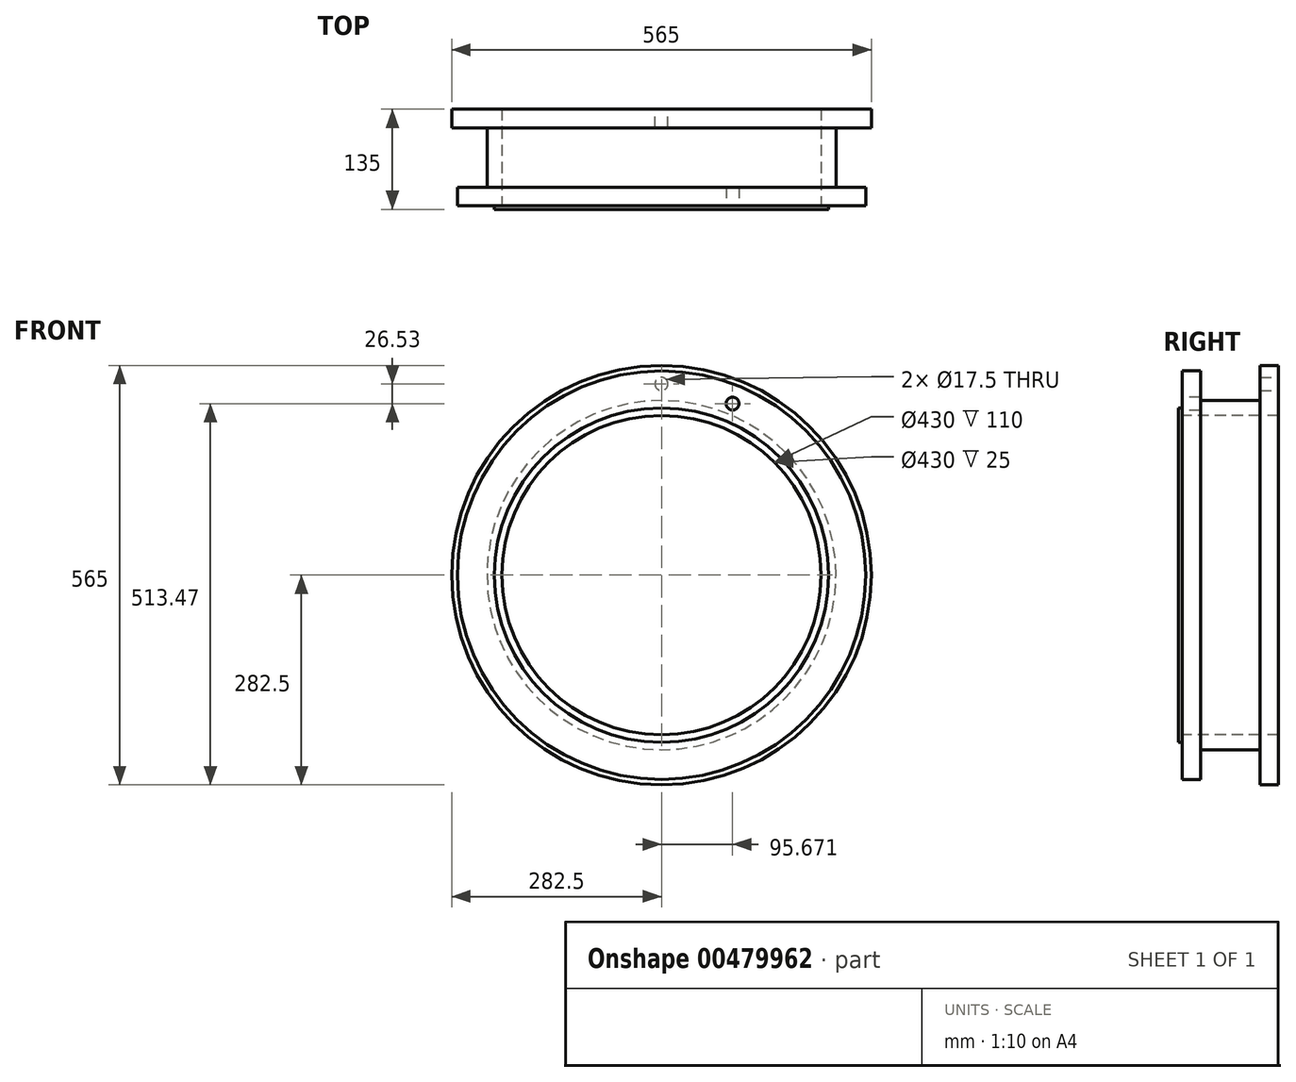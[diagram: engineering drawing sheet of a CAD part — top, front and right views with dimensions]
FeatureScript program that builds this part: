
annotation { "Feature Type Name" : "Feature", "Feature Type Description" : "" }
export const myFeature = defineFeature(function(context is Context, id is Id, definition is map)
    precondition{}
    {
        {
            var Q0;
            Q0=qCreatedBy(makeId("Front.planeOp"),FACE);
            var sketch = newSketch(context, id + "F0", { "sketchPlane" : qUnion([Q0])});
            skCircle(sketch, "E0", {"center": v(0, 0) * mm, "radius": 275 * mm});
            skSolve(sketch);
        }
        {
            var Q0;
            Q0=makeQuery(id+"F0.imprint","IMPRINT",FACE,{"disambiguationData":[TD([[makeQuery(id+"F0.imprint","IMPRINT",EDGE,{"derivedFrom":sQuery(id+"F0.wireOp",EDGE,"E0")}),1.0]])]});
            extrude(context, id + "F1", {"entities" : qUnion([Q0]), "depth" : 25 * mm});
        }
        {
            var Q0;
            Q0=makeQuery(id+"F1.opExtrude","CAP_FACE",FACE,{"disambiguationData":[OSD([sQuery(id+"F0.wireOp",EDGE,"E0")])],"isStart":false});
            var sketch = newSketch(context, id + "F2", { "sketchPlane" : qUnion([Q0])});
            skCircle(sketch, "E1", {"center": v(0, 0) * mm, "radius": 250 * mm, "construction": true});
            skLineSegment(sketch, "E2", {"start": v(95.67, 230.97) * mm, "end": v(0, 0) * mm, "construction": true});
            skLineSegment(sketch, "E3", {"start": v(0, 0) * mm, "end": v(0, 250) * mm, "construction": true});
            skSolve(sketch);
        }
        {
            var Q0;
            Q0=sQuery(id+"F2.wireOp",VERTEX,"E2.start");
            var Q1;
            Q1=makeQuery(id+"F1.opExtrude","SWEPT_BODY",BODY,{"disambiguationData":[OSD([sQuery(id+"F0.wireOp",EDGE,"E0")])]});
            hole(context, id + "F3", {"style" : HoleStyle.SIMPLE, "endStyle" : HoleEndStyle.THROUGH, "holeDiameter" : 17.5 * mm, "isTappedThrough" : true, "tappedDepth" : 12 * mm, "tapClearance" : 3, "locations" : qUnion([Q0]), "scope" : qUnion([Q1])});
        }
        {
            var Q0;
            Q0=makeQuery(id+"F1.opExtrude","CAP_FACE",FACE,{"disambiguationData":[OSD([sQuery(id+"F0.wireOp",EDGE,"E0")])],"isStart":false});
            var sketch = newSketch(context, id + "F4", { "sketchPlane" : qUnion([Q0])});
            skCircle(sketch, "E4", {"center": v(0, 0) * mm, "radius": 225 * mm});
            skSolve(sketch);
        }
        {
            var Q0;
            Q0=makeQuery(id+"F4.imprint","IMPRINT",FACE,{"disambiguationData":[TD([[makeQuery(id+"F4.imprint","IMPRINT",EDGE,{"derivedFrom":sQuery(id+"F4.wireOp",EDGE,"E4")}),1.0]])]});
            extrude(context, id + "F5", {"entities" : qUnion([Q0]), "operationType" : NewBodyOperationType.ADD, "depth" : 5 * mm});
        }
        {
            var Q0;
            Q0=makeQuery(id+"F5.opExtrude","CAP_FACE",FACE,{"disambiguationData":[OSD([sQuery(id+"F4.wireOp",EDGE,"E4")])],"isStart":false});
            var sketch = newSketch(context, id + "F6", { "sketchPlane" : qUnion([Q0])});
            skCircle(sketch, "E5", {"center": v(0, 0) * mm, "radius": 215 * mm});
            skSolve(sketch);
        }
        {
            var Q0;
            Q0=makeQuery(id+"F6.imprint","IMPRINT",FACE,{"disambiguationData":[TD([[makeQuery(id+"F6.imprint","IMPRINT",EDGE,{"derivedFrom":sQuery(id+"F6.wireOp",EDGE,"E5")}),1.0]])]});
            extrude(context, id + "F7", {"entities" : qUnion([Q0]), "operationType" : NewBodyOperationType.REMOVE, "endBound" : BoundingType.THROUGH_ALL, "oppositeDirection" : true, "depth" : 25 * mm});
        }
        {
            var Q0;
            Q0=makeQuery(id+"F1.opExtrude","CAP_FACE",FACE,{"disambiguationData":[OSD([sQuery(id+"F0.wireOp",EDGE,"E0")])],"isStart":true});
            var sketch = newSketch(context, id + "F8", { "sketchPlane" : qUnion([Q0])});
            skCircle(sketch, "E6", {"center": v(0, 0) * mm, "radius": 235 * mm});
            skSolve(sketch);
        }
        {
            var Q0;
            Q0=makeQuery(id+"F8.imprint","IMPRINT",FACE,{"disambiguationData":[TD([[makeQuery(id+"F8.imprint","IMPRINT",EDGE,{"derivedFrom":sQuery(id+"F8.wireOp",EDGE,"E6")}),1.0]])]});
            extrude(context, id + "F9", {"entities" : qUnion([Q0]), "operationType" : NewBodyOperationType.ADD, "depth" : 80 * mm});
        }
        {
            var Q0;
            Q0=makeQuery(id+"F9.opExtrude","CAP_FACE",FACE,{"disambiguationData":[OSD([sQuery(id+"F0.wireOp",EDGE,"E0"),sQuery(id+"F6.wireOp",EDGE,"E5"),sQuery(id+"F8.wireOp",EDGE,"E6")])],"isStart":false});
            var sketch = newSketch(context, id + "F10", { "sketchPlane" : qUnion([Q0])});
            skCircle(sketch, "E7", {"center": v(0, 0) * mm, "radius": 282.5 * mm});
            skSolve(sketch);
        }
        {
            var Q0;
            Q0=makeQuery(id+"F10.imprint","IMPRINT",FACE,{"disambiguationData":[TD([[makeQuery(id+"F10.imprint","IMPRINT",EDGE,{"derivedFrom":sQuery(id+"F10.wireOp",EDGE,"E7")}),1.0]])]});
            var Q1;
            Q1=makeQuery(id+"F10.imprint","IMPRINT",FACE,{"disambiguationData":[TD([[makeQuery(id+"F10.imprint","IMPRINT",EDGE,{"derivedFrom":makeQuery(id+"F9.opExtrude","CAP_EDGE",EDGE,{"disambiguationData":[OSD([sQuery(id+"F8.wireOp",EDGE,"E6")])],"isStart":false})}),1.0]])]});
            extrude(context, id + "F11", {"entities" : qUnion([Q0, Q1]), "depth" : 25 * mm});
        }
        {
            var Q0;
            Q0=makeQuery(id+"F11.opExtrude","CAP_FACE",FACE,{"disambiguationData":[OSD([sQuery(id+"F0.wireOp",EDGE,"E0"),sQuery(id+"F6.wireOp",EDGE,"E5"),sQuery(id+"F10.wireOp",EDGE,"E7")])],"isStart":false});
            var sketch = newSketch(context, id + "F12", { "sketchPlane" : qUnion([Q0])});
            skCircle(sketch, "E8", {"center": v(0, 0) * mm, "radius": 257.5 * mm, "construction": true});
            skLineSegment(sketch, "E9", {"start": v(0, 0) * mm, "end": v(0, 257.5) * mm, "construction": true});
            skSolve(sketch);
        }
        {
            var Q0;
            Q0=sQuery(id+"F12.wireOp",VERTEX,"E9.end");
            var Q1;
            Q1=makeQuery(id+"F11.opExtrude","SWEPT_BODY",BODY,{"disambiguationData":[OSD([sQuery(id+"F0.wireOp",EDGE,"E0"),sQuery(id+"F6.wireOp",EDGE,"E5"),sQuery(id+"F10.wireOp",EDGE,"E7")])]});
            hole(context, id + "F13", {"style" : HoleStyle.SIMPLE, "endStyle" : HoleEndStyle.BLIND, "holeDiameter" : 17.5 * mm, "holeDepth" : 25 * mm, "isTappedThrough" : true, "tappedDepth" : 12 * mm, "tapClearance" : 3, "locations" : qUnion([Q0]), "scope" : qUnion([Q1])});
        }
    });
